# Revit family: WH1830A-SLPT
name_source: partatom
category: Mechanical Equipment
revit_build: Autodesk Revit MEP 2016 (Build: 20150220_1215(x64)
units: mm (PartAtom-declared; Revit-internal decimal feet)

## family parameters
Cut with Voids When Loaded = No
Host = Face
OmniClass Number = 23.40.95.17.31
OmniClass Title = Wall Hangings
Part Type = Normal
Room Calculation Point = No
Round Connector Dimension = Use Diameter
Shared = Yes

## types (1)
- WH1830A-SLPT
    Amperage = 0
    CW Connection = No
    Default Elevation = 36 "
    Description = WH1830A-SLPT - Ligature-Resistant Adjustable Auto Release Clothes Towel Hook Front Mount White
    HW Connection = No
    Manufacturer = Whitehall Mfg
    Material = Stainless Steel
    Model = WH1830A-SLPT
    OVERALL DEPTH = 5.12
    OVERALL SIZE HEIGHT = 0.87
    OVERALL SIZE WIDTH = 5.12
    Revised Date = 10/09/2019
    Tempered Water Connection = No
    URL = https://www.whitehallmfg.com
    Vent Connection = No
    Voltage = 0
    Waste Connection = No

## geometry (parser evidence)
native form markers: Sweep x3
no freeform markers — native parametric forms only
